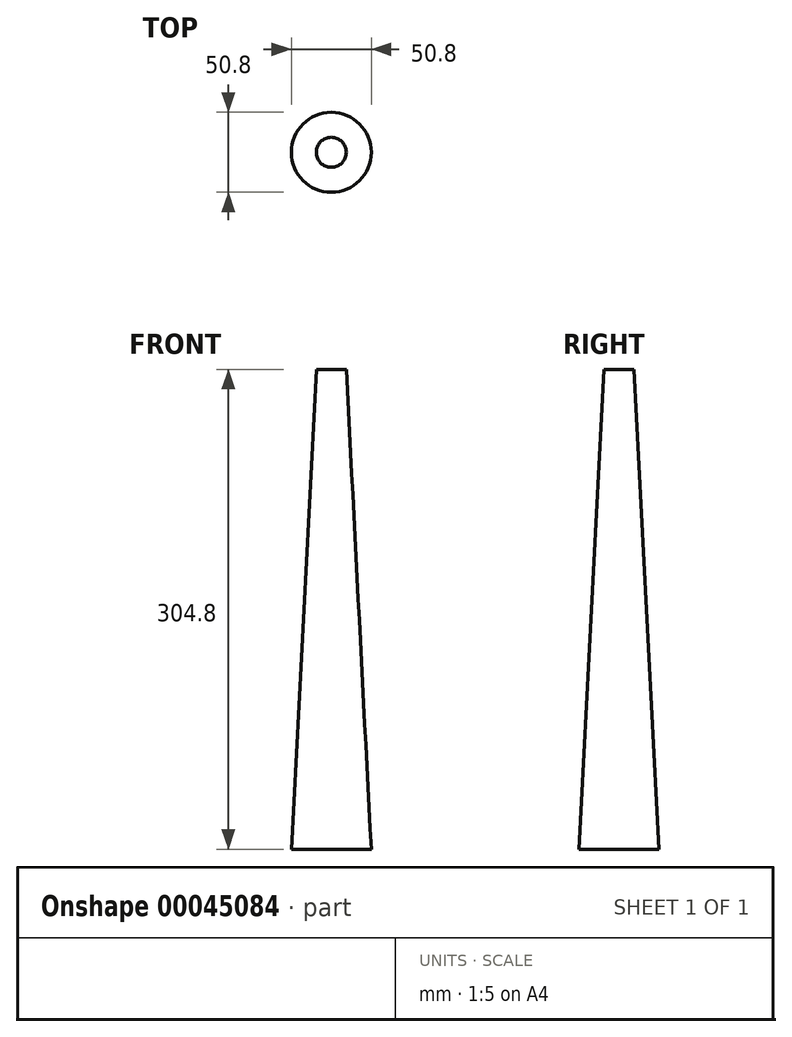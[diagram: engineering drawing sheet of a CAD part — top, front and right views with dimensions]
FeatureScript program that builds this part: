
annotation { "Feature Type Name" : "Feature", "Feature Type Description" : "" }
export const myFeature = defineFeature(function(context is Context, id is Id, definition is map)
    precondition{}
    {
        {
            var Q0;
            Q0=qCreatedBy(makeId("Top.planeOp"),FACE);
            var sketch = newSketch(context, id + "F0", { "sketchPlane" : qUnion([Q0])});
            skCircle(sketch, "E0", {"center": v(0, 0) * mm, "radius": 25.4 * mm});
            skLineSegment(sketch, "E1", {"start": v(-25.4, 0) * mm, "end": v(25.4, 0) * mm, "construction": true});
            skSolve(sketch);
        }
        {
            var Q0;
            Q0 = qSketchRegion(id + "F0", true);
            extrude(context, id + "F1", {"entities" : qUnion([Q0]), "depth" : 304.8 * mm});
        }
        {
            var Q0;
            Q0=makeQuery(id+"F1.opExtrude","CAP_FACE",FACE,{"disambiguationData":[OSD([sQuery(id+"F0.wireOp",EDGE,"E0")])],"isStart":false});
            var sketch = newSketch(context, id + "F2", { "sketchPlane" : qUnion([Q0])});
            skCircle(sketch, "E2", {"center": v(0, 0) * mm, "radius": 9.53 * mm});
            skSolve(sketch);
        }
        {
            var Q1;
            Q1=makeQuery(id+"F2.imprint","IMPRINT",FACE,{"disambiguationData":[TD([[makeQuery(id+"F2.imprint","IMPRINT",EDGE,{"derivedFrom":sQuery(id+"F2.wireOp",EDGE,"E2")}),1.0]])]});
            var Q2;
            Q2=makeQuery(id+"F1.opExtrude","CAP_FACE",FACE,{"disambiguationData":[OSD([sQuery(id+"F0.wireOp",EDGE,"E0")])],"isStart":true});
            loft(context, id + "F3", {"operationType" : NewBodyOperationType.INTERSECT, "sheetProfilesArray" : [{ "sheetProfileEntities" : qUnion([Q1]) }, { "sheetProfileEntities" : qUnion([Q2]) }]});
        }
    });
